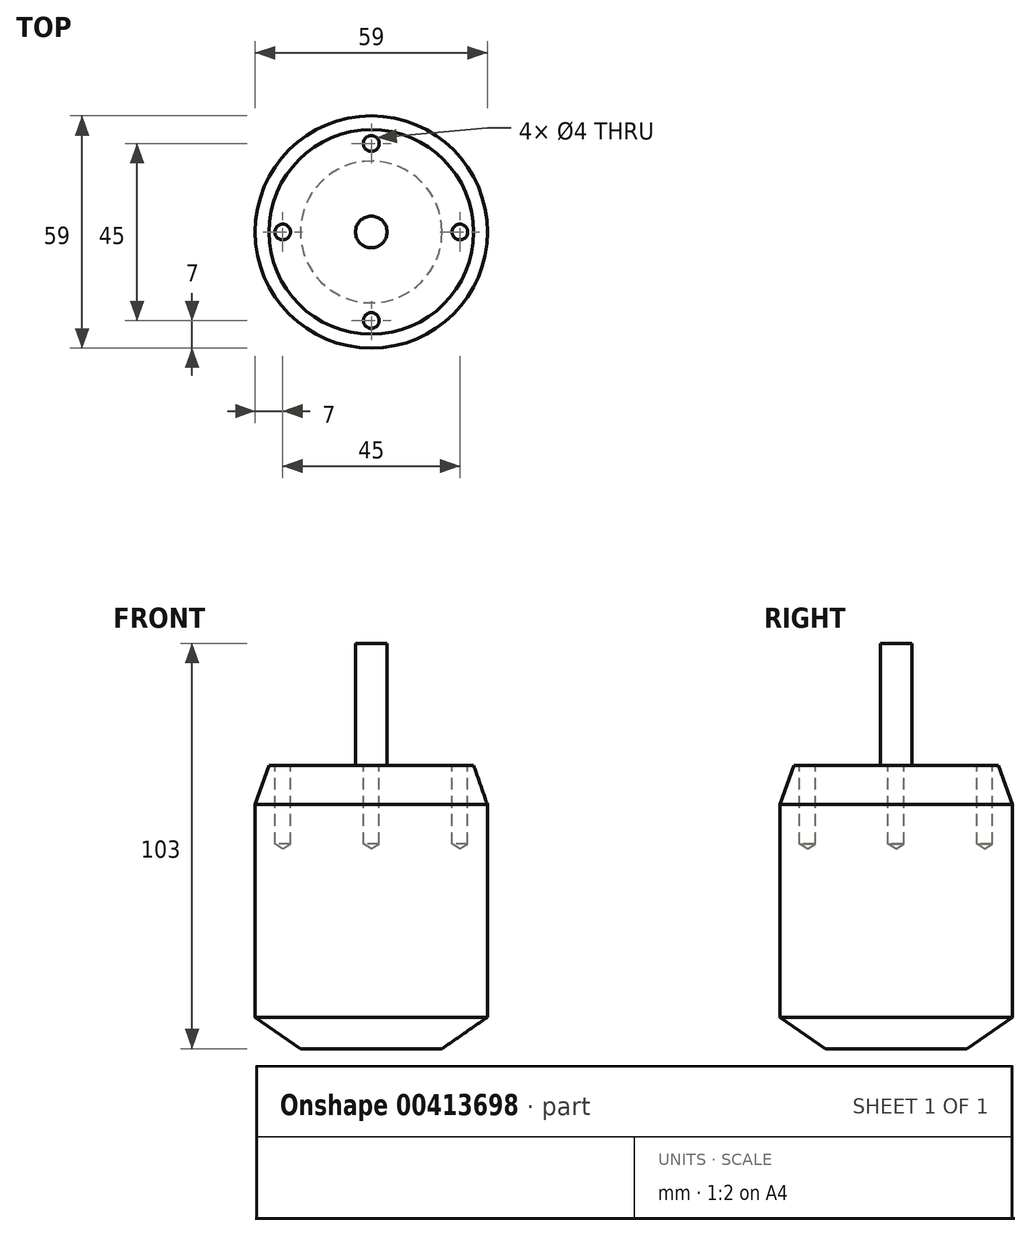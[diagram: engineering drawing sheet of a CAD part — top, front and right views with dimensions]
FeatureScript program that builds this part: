
annotation { "Feature Type Name" : "Feature", "Feature Type Description" : "" }
export const myFeature = defineFeature(function(context is Context, id is Id, definition is map)
    precondition{}
    {
        {
            var Q0;
            Q0=qCreatedBy(makeId("Top.planeOp"),FACE);
            var sketch = newSketch(context, id + "F0", { "sketchPlane" : qUnion([Q0])});
            skCircle(sketch, "E0", {"center": v(0, 0) * mm, "radius": 29.5 * mm});
            skSolve(sketch);
        }
        {
            var Q0;
            Q0=qSketchRegion(id+"F0",true);
            extrude(context, id + "F1", {"entities" : qUnion([Q0]), "depth" : 72 * mm});
        }
        {
            var Q0;
            Q0=makeQuery(id+"F1.opExtrude","CAP_FACE",FACE,{"disambiguationData":[OSD([sQuery(id+"F0.wireOp",EDGE,"E0")])],"isStart":false});
            chamfer(context, id + "F2", {"entities" : qUnion([Q0]), "chamferType" : ChamferType.TWO_OFFSETS, "width1" : 3.5 * mm, "oppositeDirection" : false, "width2" : 10 * mm, "tangentPropagation" : true});
        }
        {
            var Q0;
            Q0=makeQuery(id+"F1.opExtrude","CAP_FACE",FACE,{"disambiguationData":[OSD([sQuery(id+"F0.wireOp",EDGE,"E0")])],"isStart":true});
            chamfer(context, id + "F3", {"entities" : qUnion([Q0]), "chamferType" : ChamferType.TWO_OFFSETS, "width1" : 8 * mm, "oppositeDirection" : false, "width2" : 11.5 * mm, "tangentPropagation" : true});
        }
        {
            var Q0;
            Q0=qCreatedBy(makeId("Top.planeOp"),FACE);
            var sketch = newSketch(context, id + "F4", { "sketchPlane" : qUnion([Q0])});
            skCircle(sketch, "E1", {"center": v(0, 0) * mm, "radius": 4 * mm});
            skSolve(sketch);
        }
        {
            var Q0;
            Q0=makeQuery(id+"F4.imprint","IMPRINT",FACE,{"disambiguationData":[TD([[makeQuery(id+"F4.imprint","IMPRINT",EDGE,{"derivedFrom":sQuery(id+"F4.wireOp",EDGE,"E1")}),1.0]])]});
            extrude(context, id + "F5", {"entities" : qUnion([Q0]), "operationType" : NewBodyOperationType.ADD, "depth" : 103 * mm});
        }
        {
            var Q0;
            Q0=makeQuery(id+"F1.opExtrude","CAP_FACE",FACE,{"disambiguationData":[OSD([sQuery(id+"F0.wireOp",EDGE,"E0")])],"isStart":false});
            var sketch = newSketch(context, id + "F6", { "sketchPlane" : qUnion([Q0])});
            skCircle(sketch, "E2", {"center": v(0, 0) * mm, "radius": 22.5 * mm});
            skPoint(sketch, "E3", {"position": v(0, 22.5) * mm});
            skPoint(sketch, "E4", {"position": v(22.5, 0) * mm});
            skPoint(sketch, "E5", {"position": v(0, -22.5) * mm});
            skPoint(sketch, "E6", {"position": v(-22.5, 0) * mm});
            skSolve(sketch);
        }
        {
            var Q0;
            Q0=sQuery(id+"F6.wireOp",VERTEX,"E3");
            var Q1;
            Q1=sQuery(id+"F6.wireOp",VERTEX,"E4");
            var Q2;
            Q2=sQuery(id+"F6.wireOp",VERTEX,"E5");
            var Q3;
            Q3=sQuery(id+"F6.wireOp",VERTEX,"E6");
            var Q4;
            Q4=makeQuery(id+"F1.opExtrude","SWEPT_BODY",BODY,{"disambiguationData":[OSD([sQuery(id+"F0.wireOp",EDGE,"E0")])]});
            hole(context, id + "F7", {"style" : HoleStyle.SIMPLE, "holeDiameter" : 4 * mm, "endStyle" : HoleEndStyle.BLIND, "holeDepth" : 20 * mm, "locations" : qUnion([Q0, Q1, Q2, Q3]), "scope" : qUnion([Q4]), "tappedDepth" : 12 * mm, "tapClearance" : 3});
        }
    });
